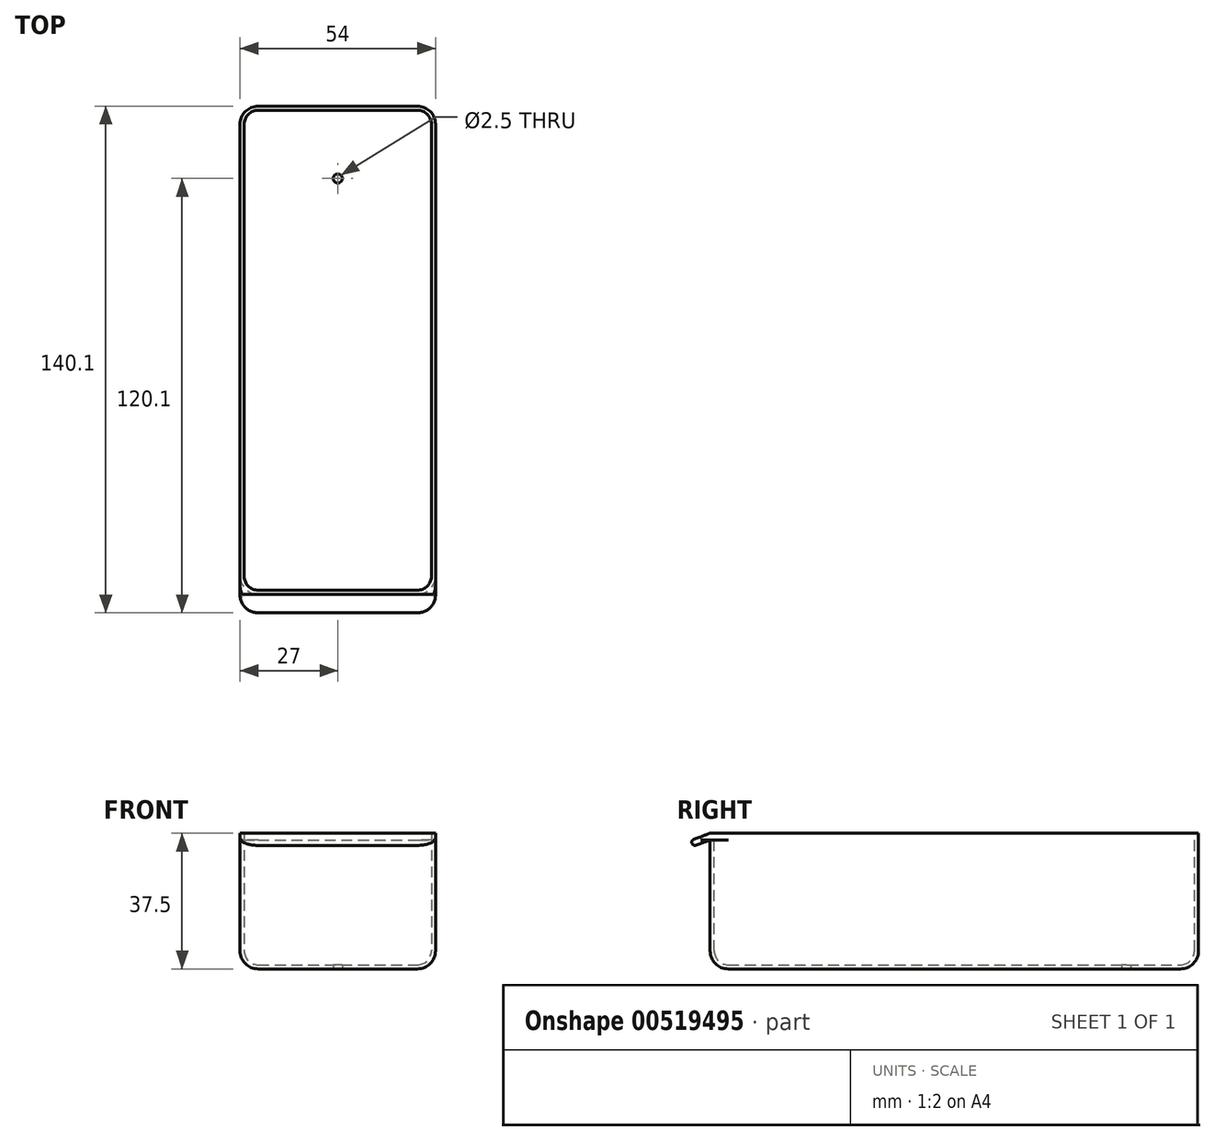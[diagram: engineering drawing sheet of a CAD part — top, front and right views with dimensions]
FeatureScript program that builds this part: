
annotation { "Feature Type Name" : "Feature", "Feature Type Description" : "" }
export const myFeature = defineFeature(function(context is Context, id is Id, definition is map)
    precondition{}
    {
        {
            var Q0;
            Q0=qCreatedBy(makeId("Top.planeOp"),FACE);
            var sketch = newSketch(context, id + "F0", { "sketchPlane" : qUnion([Q0])});
            skLineSegment(sketch, "E0.bottom", {"start": v(-27, 67.5) * mm, "end": v(27, 67.5) * mm});
            skLineSegment(sketch, "E0.top", {"start": v(-27, -67.5) * mm, "end": v(27, -67.5) * mm});
            skLineSegment(sketch, "E0.left", {"start": v(-27, 67.5) * mm, "end": v(-27, -67.5) * mm});
            skLineSegment(sketch, "E0.right", {"start": v(27, 67.5) * mm, "end": v(27, -67.5) * mm});
            skSolve(sketch);
        }
        {
            var Q0;
            Q0 = qSketchRegion(id + "F0", true);
            extrude(context, id + "F1", {"entities" : qUnion([Q0]), "depth" : (35 + 2.5) * mm, "offsetDistance" : 25 * mm});
        }
        {
            var Q0;
            Q0=makeQuery(id+"F1.opExtrude","CAP_FACE",FACE,{"disambiguationData":[OSD([sQuery(id+"F0.wireOp",EDGE,"E0.bottom"),sQuery(id+"F0.wireOp",EDGE,"E0.top"),sQuery(id+"F0.wireOp",EDGE,"E0.left"),sQuery(id+"F0.wireOp",EDGE,"E0.right")])],"isStart":true});
            var Q1;
            Q1=makeQuery(id+"F1.opExtrude","SWEPT_EDGE",EDGE,{"disambiguationData":[OSD([sQuery(id+"F0.wireOp",EDGE,"E0.bottom"),sQuery(id+"F0.wireOp",EDGE,"E0.right")])]});
            var Q2;
            Q2=makeQuery(id+"F1.opExtrude","SWEPT_EDGE",EDGE,{"disambiguationData":[OSD([sQuery(id+"F0.wireOp",EDGE,"E0.bottom"),sQuery(id+"F0.wireOp",EDGE,"E0.left")])]});
            var Q3;
            Q3=makeQuery(id+"F1.opExtrude","SWEPT_EDGE",EDGE,{"disambiguationData":[OSD([sQuery(id+"F0.wireOp",EDGE,"E0.top"),sQuery(id+"F0.wireOp",EDGE,"E0.left")])]});
            var Q4;
            Q4=makeQuery(id+"F1.opExtrude","SWEPT_EDGE",EDGE,{"disambiguationData":[OSD([sQuery(id+"F0.wireOp",EDGE,"E0.top"),sQuery(id+"F0.wireOp",EDGE,"E0.right")])]});
            fillet(context, id + "F2", {"entities" : qUnion([Q0, Q1, Q2, Q3, Q4]), "radius" : 5 * mm, "tangentPropagation" : true, "allowEdgeOverflow" : false});
        }
        {
            var Q0;
            {var subQ0=sQuery(id+"F4.wireOp",EDGE,"E3");Q0=makeQuery(id+"F6.boolean.opBoolean","MERGE",FACE,{"derivedFrom":[makeQuery(id+"F5.boolean.opBoolean","MERGE",FACE,{"derivedFrom":[makeQuery(id+"F1.opExtrude","CAP_FACE",FACE,{"disambiguationData":[OSD([sQuery(id+"F0.wireOp",EDGE,"E0.bottom"),sQuery(id+"F0.wireOp",EDGE,"E0.top"),sQuery(id+"F0.wireOp",EDGE,"E0.left"),sQuery(id+"F0.wireOp",EDGE,"E0.right")])],"isStart":false}),makeQuery(id+"F5.opExtrude","SWEPT_FACE",FACE,{"disambiguationData":[OSD([subQ0])]})]}),makeQuery(id+"F6.opExtrude","SWEPT_FACE",FACE,{"disambiguationData":[OSD([subQ0])]})]});}
            shell(context, id + "F3", {"entities" : qUnion([Q0]), "thickness" : 1.12 * mm});
        }
        {
            var Q0;
            Q0=qCreatedBy(makeId("Right.planeOp"),FACE);
            var sketch = newSketch(context, id + "F4", { "sketchPlane" : qUnion([Q0])});
            skLineSegment(sketch, "E1.0", {"start": v(-62.5, 37.5) * mm, "end": v(-67.5, 37.5) * mm, "construction": true});
            skLineSegment(sketch, "E2.0", {"start": v(-67.5, 37.5) * mm, "end": v(-67.5, 5) * mm, "construction": true});
            skLineSegment(sketch, "E3", {"start": v(-62.5, 37.5) * mm, "end": v(-67.5, 37.5) * mm});
            skLineSegment(sketch, "E4", {"start": v(-72.84, 35.55) * mm, "end": v(-67.5, 37.5) * mm});
            skLineSegment(sketch, "E5", {"start": v(-72.84, 35.55) * mm, "end": v(-72.25, 33.91) * mm});
            skLineSegment(sketch, "E6", {"start": v(-72.25, 33.91) * mm, "end": v(-67.5, 35.64) * mm});
            skLineSegment(sketch, "E7", {"start": v(-67.5, 35.64) * mm, "end": v(-62.5, 35.64) * mm});
            skLineSegment(sketch, "E8", {"start": v(-62.5, 35.64) * mm, "end": v(-62.5, 37.5) * mm});
            skSolve(sketch);
        }
        {
            var Q0;
            Q0=makeQuery(id+"F4.imprint","IMPRINT",FACE,{"disambiguationData":[TD([[makeQuery(id+"F4.imprint","IMPRINT",EDGE,{"derivedFrom":sQuery(id+"F4.wireOp",EDGE,"E3")}),1.0]])]});
            var Q1;
            Q1=makeQuery(id+"F1.opExtrude","SWEPT_FACE",FACE,{"disambiguationData":[OSD([sQuery(id+"F0.wireOp",EDGE,"E0.left")])]});
            extrude(context, id + "F5", {"entities" : qUnion([Q0]), "operationType" : NewBodyOperationType.ADD, "endBound" : BoundingType.UP_TO_SURFACE, "oppositeDirection" : true, "depth" : 25 * mm, "endBoundEntityFace" : qUnion([Q1]), "offsetDistance" : 25 * mm});
        }
        {
            var Q0;
            Q0 = qSketchRegion(id + "F4", true);
            var Q1;
            Q1=makeQuery(id+"F1.opExtrude","SWEPT_FACE",FACE,{"disambiguationData":[OSD([sQuery(id+"F0.wireOp",EDGE,"E0.right")])]});
            extrude(context, id + "F6", {"entities" : qUnion([Q0]), "operationType" : NewBodyOperationType.ADD, "endBound" : BoundingType.UP_TO_SURFACE, "depth" : 25 * mm, "endBoundEntityFace" : qUnion([Q1]), "offsetDistance" : 25 * mm});
        }
        {
            var Q0;
            Q0=makeQuery(id+"F5.opExtrude","CAP_EDGE",EDGE,{"disambiguationData":[OSD([sQuery(id+"F4.wireOp",EDGE,"E5")])],"isStart":false});
            var Q1;
            Q1=makeQuery(id+"F6.opExtrude","CAP_EDGE",EDGE,{"disambiguationData":[OSD([sQuery(id+"F4.wireOp",EDGE,"E5")])],"isStart":false});
            fillet(context, id + "F7", {"entities" : qUnion([Q0, Q1]), "radius" : 5 * mm, "tangentPropagation" : true, "allowEdgeOverflow" : false});
        }
        {
            var Q0;
            {var subQ0=sQuery(id+"F4.wireOp",EDGE,"E5");var subQ1=sQuery(id+"F4.wireOp",EDGE,"E4");Q0=makeQuery(id+"F6.boolean.opBoolean","MERGE",EDGE,{"derivedFrom":[makeQuery(id+"F5.opExtrude","SWEPT_EDGE",EDGE,{"disambiguationData":[OSD([subQ1,subQ0])]}),makeQuery(id+"F6.opExtrude","SWEPT_EDGE",EDGE,{"disambiguationData":[OSD([subQ1,subQ0])]})]});}
            var Q1;
            {var subQ0=sQuery(id+"F4.wireOp",EDGE,"E6");var subQ1=sQuery(id+"F4.wireOp",EDGE,"E5");Q1=makeQuery(id+"F6.boolean.opBoolean","MERGE",EDGE,{"derivedFrom":[makeQuery(id+"F5.opExtrude","SWEPT_EDGE",EDGE,{"disambiguationData":[OSD([subQ1,subQ0])]}),makeQuery(id+"F6.opExtrude","SWEPT_EDGE",EDGE,{"disambiguationData":[OSD([subQ1,subQ0])]})]});}
            fillet(context, id + "F8", {"entities" : qUnion([Q0, Q1]), "radius" : (1.75 / 2) * mm, "tangentPropagation" : true, "allowEdgeOverflow" : false});
        }
        {
            var Q0;
            Q0=makeQuery(id+"F3.opShell","OFFSET_FACE",FACE,{"disambiguationData":[OSD([sQuery(id+"F0.wireOp",EDGE,"E0.bottom"),sQuery(id+"F0.wireOp",EDGE,"E0.top"),sQuery(id+"F0.wireOp",EDGE,"E0.left"),sQuery(id+"F0.wireOp",EDGE,"E0.right")])]});
            cPlane(context, id + "F9", {"entities" : qUnion([Q0]), "cplaneType" : CPlaneType.OFFSET, "offset" : 25 * mm, "width" : 150 * mm, "height" : 150 * mm});
        }
        {
            var Q0;
            Q0=qCreatedBy(id+"F9.planeOp",FACE);
            var sketch = newSketch(context, id + "F10", { "sketchPlane" : qUnion([Q0])});
            skLineSegment(sketch, "E9.0.0", {"start": v(-22, -66.38) * mm, "end": v(22, -66.38) * mm});
            skLineSegment(sketch, "E9.0.2", {"start": v(-22, -66.38) * mm, "end": v(22, -66.38) * mm});
            skLineSegment(sketch, "E10.0.0", {"start": v(25.87, -62.5) * mm, "end": v(25.88, 62.5) * mm});
            skLineSegment(sketch, "E10.0.2", {"start": v(25.88, 62.5) * mm, "end": v(25.87, -62.5) * mm});
            skLineSegment(sketch, "E11.0.0", {"start": v(-25.87, 62.5) * mm, "end": v(-25.88, -62.5) * mm});
            skLineSegment(sketch, "E11.0.2", {"start": v(-25.87, 62.5) * mm, "end": v(-25.88, -62.5) * mm});
            skLineSegment(sketch, "E12.0.0", {"start": v(22, 66.37) * mm, "end": v(-22, 66.38) * mm});
            skLineSegment(sketch, "E12.0.2", {"start": v(-22, 66.38) * mm, "end": v(22, 66.37) * mm});
            skArc(sketch, "E13.0", {"start": v(-25.87, 62.5) * mm, "mid": v(-24.74, 65.24) * mm, "end": v(-22, 66.38) * mm});
            skArc(sketch, "E14.0", {"start": v(22, 66.37) * mm, "mid": v(24.74, 65.24) * mm, "end": v(25.88, 62.5) * mm});
            skArc(sketch, "E15.0", {"start": v(25.87, -62.5) * mm, "mid": v(24.74, -65.24) * mm, "end": v(22, -66.38) * mm});
            skArc(sketch, "E16.0", {"start": v(-25.88, -62.5) * mm, "mid": v(-24.74, -65.24) * mm, "end": v(-22, -66.38) * mm});
            skSolve(sketch);
        }
        {
            var Q0;
            Q0 = qSketchRegion(id + "F10", true);
            extrude(context, id + "F11", {"entities" : qUnion([Q0]), "operationType" : NewBodyOperationType.REMOVE, "endBound" : BoundingType.THROUGH_ALL, "depth" : 25 * mm, "offsetDistance" : 25 * mm});
        }
        {
            var Q0;
            Q0=makeQuery(id+"F1.opExtrude","CAP_FACE",FACE,{"disambiguationData":[OSD([sQuery(id+"F0.wireOp",EDGE,"E0.bottom"),sQuery(id+"F0.wireOp",EDGE,"E0.top"),sQuery(id+"F0.wireOp",EDGE,"E0.left"),sQuery(id+"F0.wireOp",EDGE,"E0.right")])],"isStart":true});
            var sketch = newSketch(context, id + "F12", { "sketchPlane" : qUnion([Q0])});
            skPoint(sketch, "E17", {"position": v(0, -47.5) * mm});
            skSolve(sketch);
        }
        {
            var Q0;
            Q0=sQuery(id+"F12.wireOp",VERTEX,"E17");
            var Q1;
            Q1=makeQuery(id+"F1.opExtrude","SWEPT_BODY",BODY,{"disambiguationData":[OSD([sQuery(id+"F0.wireOp",EDGE,"E0.bottom"),sQuery(id+"F0.wireOp",EDGE,"E0.top"),sQuery(id+"F0.wireOp",EDGE,"E0.left"),sQuery(id+"F0.wireOp",EDGE,"E0.right")])]});
            hole(context, id + "F13", {"style" : HoleStyle.SIMPLE, "endStyle" : HoleEndStyle.THROUGH, "holeDiameter" : 2.5 * mm, "isTappedThrough" : true, "tappedDepth" : 38.4 * mm, "tapClearance" : 3, "startFromSketch" : true, "locations" : qUnion([Q0]), "scope" : qUnion([Q1])});
        }
    });
